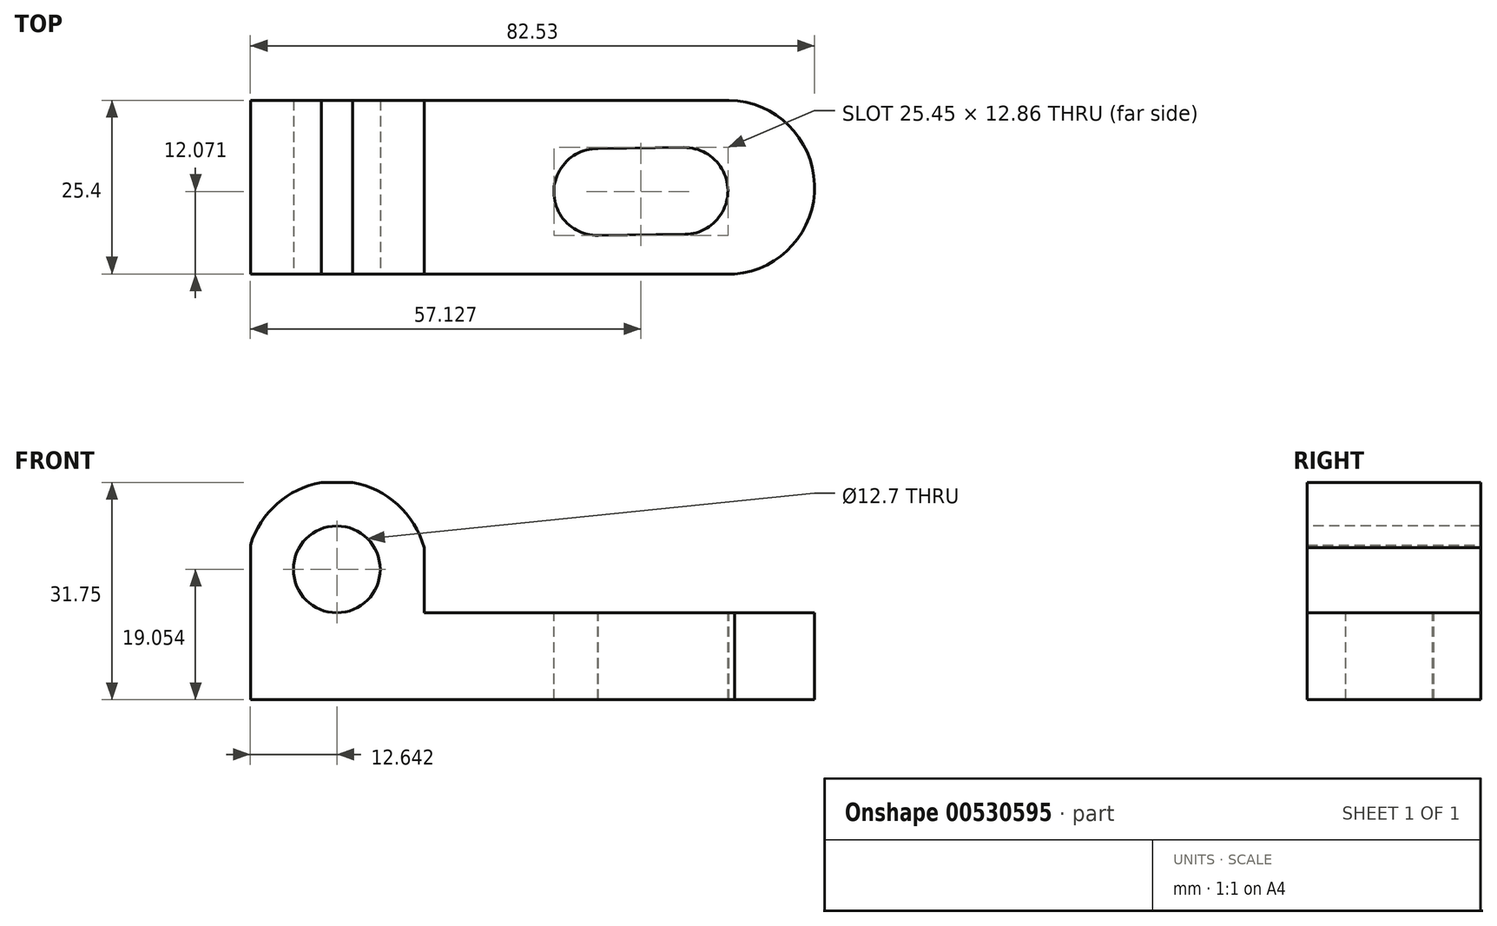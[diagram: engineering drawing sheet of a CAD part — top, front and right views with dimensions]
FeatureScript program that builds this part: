
annotation { "Feature Type Name" : "Feature", "Feature Type Description" : "" }
export const myFeature = defineFeature(function(context is Context, id is Id, definition is map)
    precondition{}
    {
        {
            var Q0;
            Q0=qCreatedBy(makeId("Front.planeOp"),FACE);
            var sketch = newSketch(context, id + "F0", { "sketchPlane" : qUnion([Q0])});
            skLineSegment(sketch, "E0", {"start": v(-63.67, 36.44) * mm, "end": v(-38.27, 36.44) * mm});
            skLineSegment(sketch, "E1", {"start": v(-38.27, 36.44) * mm, "end": v(-38.27, 17.4) * mm});
            skLineSegment(sketch, "E2", {"start": v(-38.27, 17.4) * mm, "end": v(18.88, 17.4) * mm});
            skLineSegment(sketch, "E3", {"start": v(18.88, 17.4) * mm, "end": v(18.88, 4.7) * mm});
            skLineSegment(sketch, "E4", {"start": v(18.88, 4.7) * mm, "end": v(-63.67, 4.7) * mm});
            skLineSegment(sketch, "E5", {"start": v(-63.67, 4.7) * mm, "end": v(-63.67, 36.44) * mm});
            skArc(sketch, "E6", {"start": v(-38.27, 26.92) * mm, "mid": v(-50.81, 36.64) * mm, "end": v(-63.67, 27.33) * mm});
            skSolve(sketch);
        }
        {
            var Q0;
            {var subQ0=sQuery(id+"F0.wireOp",EDGE,"E2");Q0=makeQuery(id+"F0.imprint","IMPRINT",FACE,{"disambiguationData":[TD([[makeQuery(id+"F0.imprint","IMPRINT",EDGE,{"derivedFrom":subQ0}),-1.0]])]});}
            extrude(context, id + "F1", {"entities" : qUnion([Q0]), "depth" : 25.4 * mm, "offsetDistance" : 25.4 * mm});
        }
        {
            var Q0;
            Q0=makeQuery(id+"F1.opExtrude","CAP_FACE",FACE,{"disambiguationData":[OSD([sQuery(id+"F0.wireOp",EDGE,"E0"),sQuery(id+"F0.wireOp",EDGE,"E1"),sQuery(id+"F0.wireOp",EDGE,"E2"),sQuery(id+"F0.wireOp",EDGE,"E3"),sQuery(id+"F0.wireOp",EDGE,"E4"),sQuery(id+"F0.wireOp",EDGE,"E5"),sQuery(id+"F0.wireOp",EDGE,"E6")])],"isStart":false});
            var sketch = newSketch(context, id + "F2", { "sketchPlane" : qUnion([Q0])});
            skSolve(sketch);
        }
        {
            var Q0;
            Q0=makeQuery(id+"F1.opExtrude","SWEPT_FACE",FACE,{"disambiguationData":[OSD([sQuery(id+"F0.wireOp",EDGE,"E2")])]});
            var sketch = newSketch(context, id + "F3", { "sketchPlane" : qUnion([Q0])});
            skArc(sketch, "E7", {"start": v(5.08, -25.4) * mm, "mid": v(18.86, -13.14) * mm, "end": v(5.91, 0) * mm});
            skSolve(sketch);
        }
        {
            var Q0;
            Q0 = qSketchRegion(id + "F3", true);
            var Q1;
            {var subQ1=sQuery(id+"F0.wireOp",EDGE,"E2");var subQ6=makeQuery(id+"F1.opExtrude","SWEPT_EDGE",EDGE,{"disambiguationData":[OSD([subQ1,sQuery(id+"F0.wireOp",EDGE,"E3")])]});Q1=makeQuery(id+"F3.imprint","IMPRINT",FACE,{"disambiguationData":[TD([[makeQuery(id+"F3.imprint","IMPRINT",EDGE,{"derivedFrom":subQ6}),1.0]])]});}
            extrude(context, id + "F4", {"entities" : qUnion([Q0, Q1]), "operationType" : NewBodyOperationType.REMOVE, "oppositeDirection" : true, "depth" : 25.4 * mm, "offsetDistance" : 25.4 * mm});
        }
        {
            var Q0;
            {var subQ1=sQuery(id+"F0.wireOp",EDGE,"E0");Q0=makeQuery(id+"F2.imprint","IMPRINT",FACE,{"disambiguationData":[TD([[makeQuery(id+"F2.imprint","IMPRINT",EDGE,{"derivedFrom":makeQuery(id+"F1.opExtrude","CAP_EDGE",EDGE,{"disambiguationData":[OSD([subQ1])],"isStart":false})}),-1.0]])]});}
            var sketch = newSketch(context, id + "F5", { "sketchPlane" : qUnion([Q0])});
            skCircle(sketch, "E8", {"center": v(-51.03, 23.74) * mm, "radius": 6.35 * mm});
            skSolve(sketch);
        }
        {
            var Q0;
            Q0 = qSketchRegion(id + "F5", true);
            extrude(context, id + "F6", {"entities" : qUnion([Q0]), "operationType" : NewBodyOperationType.REMOVE, "oppositeDirection" : true, "depth" : 25.4 * mm, "offsetDistance" : 25.4 * mm});
        }
        {
            var Q0;
            Q0=makeQuery(id+"F1.opExtrude","SWEPT_FACE",FACE,{"disambiguationData":[OSD([sQuery(id+"F0.wireOp",EDGE,"E2")])]});
            var sketch = newSketch(context, id + "F7", { "sketchPlane" : qUnion([Q0])});
            skCircle(sketch, "E9", {"center": v(-0.17, -13.25) * mm, "radius": 6.35 * mm});
            skCircle(sketch, "E10", {"center": v(-12.92, -13.41) * mm, "radius": 6.35 * mm});
            skLineSegment(sketch, "E11", {"start": v(-12.84, -7.06) * mm, "end": v(0, -6.9) * mm});
            skLineSegment(sketch, "E12", {"start": v(-12.92, -19.76) * mm, "end": v(0, -19.6) * mm});
            skSolve(sketch);
        }
        {
            var Q0;
            Q0 = qSketchRegion(id + "F7", true);
            extrude(context, id + "F8", {"entities" : qUnion([Q0]), "operationType" : NewBodyOperationType.REMOVE, "oppositeDirection" : true, "depth" : 25.4 * mm, "offsetDistance" : 25.4 * mm});
        }
    });
